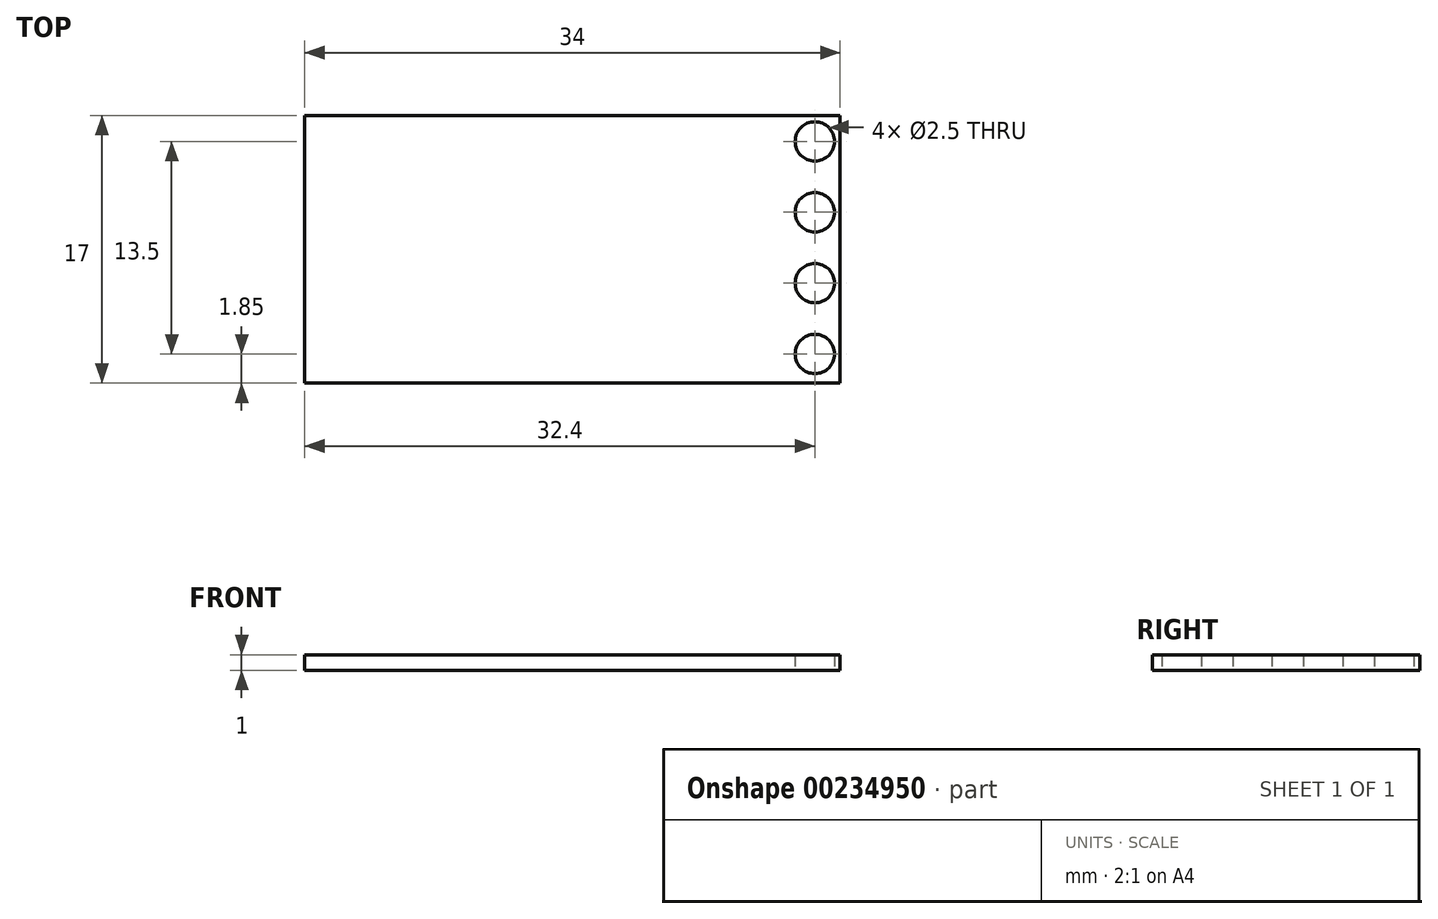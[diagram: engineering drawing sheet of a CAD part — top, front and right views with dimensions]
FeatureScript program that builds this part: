
annotation { "Feature Type Name" : "Feature", "Feature Type Description" : "" }
export const myFeature = defineFeature(function(context is Context, id is Id, definition is map)
    precondition{}
    {
        {
            var Q0;
            Q0=qCreatedBy(makeId("Top.planeOp"),FACE);
            var sketch = newSketch(context, id + "F0", { "sketchPlane" : qUnion([Q0])});
            skLineSegment(sketch, "E0.bottom", {"start": v(0, 0) * mm, "end": v(34, 0) * mm});
            skLineSegment(sketch, "E0.top", {"start": v(0, -17) * mm, "end": v(34, -17) * mm});
            skLineSegment(sketch, "E0.left", {"start": v(0, 0) * mm, "end": v(0, -17) * mm});
            skLineSegment(sketch, "E0.right", {"start": v(34, 0) * mm, "end": v(34, -17) * mm});
            skLineSegment(sketch, "E1", {"start": v(32.4, 0) * mm, "end": v(32.4, -17) * mm, "construction": true});
            skCircle(sketch, "E2", {"center": v(32.4, -15.15) * mm, "radius": 1.25 * mm});
            skCircle(sketch, "E3.0.1.0", {"center": v(32.4, -10.65) * mm, "radius": 1.25 * mm});
            skCircle(sketch, "E3.0.2.0", {"center": v(32.4, -6.15) * mm, "radius": 1.25 * mm});
            skCircle(sketch, "E3.0.3.0", {"center": v(32.4, -1.65) * mm, "radius": 1.25 * mm});
            skLineSegment(sketch, "E3.direction1", {"start": v(32.4, -15.15) * mm, "end": v(57.4, -15.15) * mm, "construction": true});
            skLineSegment(sketch, "E3.direction2", {"start": v(32.4, -15.15) * mm, "end": v(32.4, -10.65) * mm, "construction": true});
            skSolve(sketch);
        }
        {
            var Q0;
            Q0=makeQuery(id+"F0.imprint","IMPRINT",FACE,{"disambiguationData":[TD([[makeQuery(id+"F0.imprint","IMPRINT",EDGE,{"derivedFrom":sQuery(id+"F0.wireOp",EDGE,"E0.bottom")}),-1.0]])]});
            extrude(context, id + "F1", {"entities" : qUnion([Q0]), "depth" : 1 * mm});
        }
    });
